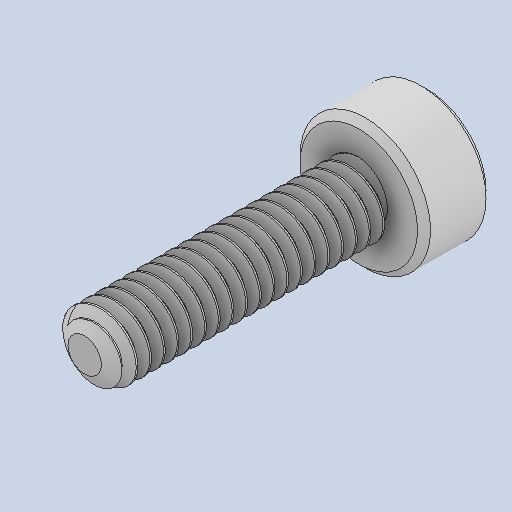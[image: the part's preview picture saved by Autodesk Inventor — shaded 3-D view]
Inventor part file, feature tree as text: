
AUTODESK INVENTOR PART (.ipt)
format: ipt  version: 2023 (Build 270158000, 158)  size: 698,880 bytes
history: native  units: mm
features: chamfer x1
ambient origin geometry x8: Origin, YZ Plane, XZ Plane, XY Plane, X Axis, Y Axis, Z Axis, Center Point
bodies: Solid1 (feature_tree)
feature tree (1):
  chamfer  "Chamfer1"  [1 undecoded]
note: 1 required parameter value undecoded (feature->parameter linkage not recoverable at this tier; creation-order binding heuristic only, values carry confidence <= 0.55)
